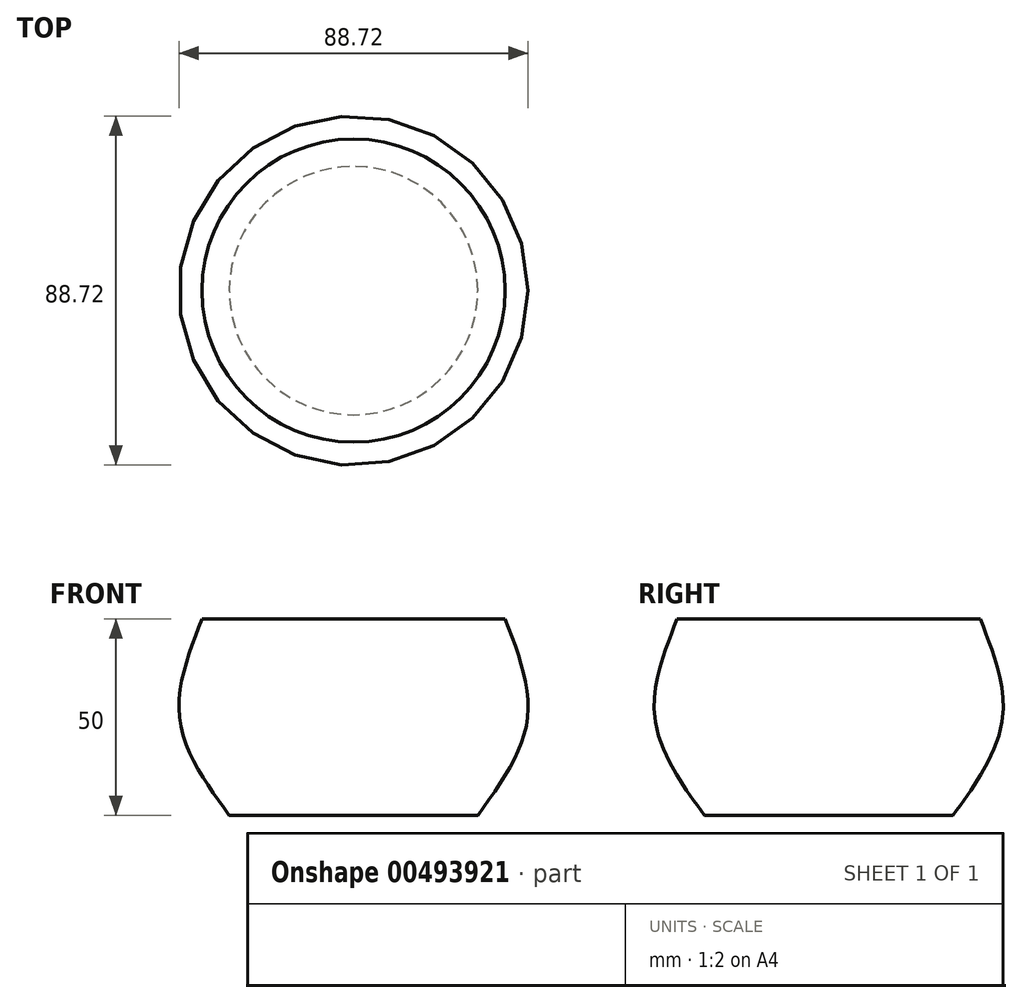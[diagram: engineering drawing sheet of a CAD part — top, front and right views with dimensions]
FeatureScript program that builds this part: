
annotation { "Feature Type Name" : "Feature", "Feature Type Description" : "" }
export const myFeature = defineFeature(function(context is Context, id is Id, definition is map)
    precondition{}
    {
        {
            var Q0;
            Q0=qCreatedBy(makeId("Top.planeOp"),FACE);
            cPlane(context, id + "F0", {"entities" : qUnion([Q0]), "cplaneType" : CPlaneType.OFFSET, "offset" : 25 * mm, "width" : 150 * mm, "height" : 150 * mm});
        }
        {
            var Q0;
            Q0=qCreatedBy(id+"F0.planeOp",FACE);
            cPlane(context, id + "F1", {"entities" : qUnion([Q0]), "cplaneType" : CPlaneType.OFFSET, "offset" : 25 * mm, "width" : 150 * mm, "height" : 150 * mm});
        }
        {
            var Q0;
            Q0=qCreatedBy(makeId("Top.planeOp"),FACE);
            var sketch = newSketch(context, id + "F2", { "sketchPlane" : qUnion([Q0])});
            skCircle(sketch, "E0", {"center": v(0, 0) * mm, "radius": 31.57 * mm});
            skSolve(sketch);
        }
        {
            var Q0;
            Q0=qCreatedBy(id+"F0.planeOp",FACE);
            var sketch = newSketch(context, id + "F3", { "sketchPlane" : qUnion([Q0])});
            skCircle(sketch, "E1", {"center": v(0, 0) * mm, "radius": 44.22 * mm});
            skSolve(sketch);
        }
        {
            var Q0;
            Q0=qCreatedBy(id+"F1.planeOp",FACE);
            var sketch = newSketch(context, id + "F4", { "sketchPlane" : qUnion([Q0])});
            skCircle(sketch, "E2", {"center": v(0, 0) * mm, "radius": 38.5 * mm});
            skSolve(sketch);
        }
        {
            var Q0;
            Q0=makeQuery(id+"F2.imprint","IMPRINT",FACE,{"disambiguationData":[TD([[makeQuery(id+"F2.imprint","IMPRINT",EDGE,{"derivedFrom":sQuery(id+"F2.wireOp",EDGE,"E0")}),1.0]])]});
            var Q1;
            Q1=makeQuery(id+"F3.imprint","IMPRINT",FACE,{"disambiguationData":[TD([[makeQuery(id+"F3.imprint","IMPRINT",EDGE,{"derivedFrom":sQuery(id+"F3.wireOp",EDGE,"E1")}),1.0]])]});
            var Q2;
            Q2=makeQuery(id+"F4.imprint","IMPRINT",FACE,{"disambiguationData":[TD([[makeQuery(id+"F4.imprint","IMPRINT",EDGE,{"derivedFrom":sQuery(id+"F4.wireOp",EDGE,"E2")}),1.0]])]});
            loft(context, id + "F5", {"sheetProfilesArray" : [{ "sheetProfileEntities" : qUnion([Q0]) }, { "sheetProfileEntities" : qUnion([Q1]) }, { "sheetProfileEntities" : qUnion([Q2]) }]});
        }
    });
